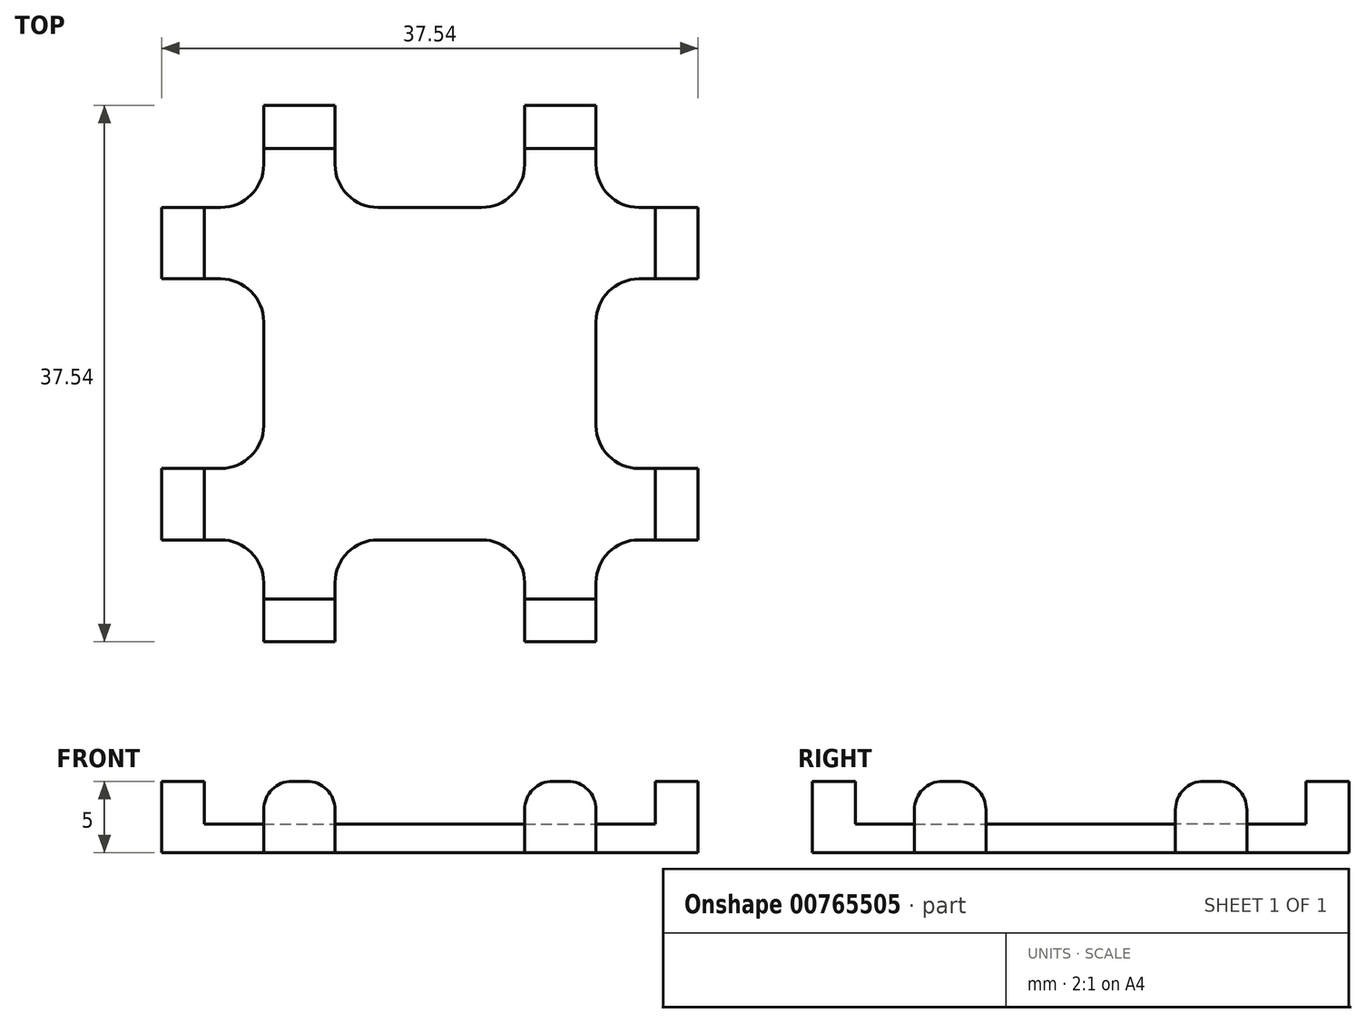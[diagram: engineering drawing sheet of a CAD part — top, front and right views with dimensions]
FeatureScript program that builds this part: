
annotation { "Feature Type Name" : "Feature", "Feature Type Description" : "" }
export const myFeature = defineFeature(function(context is Context, id is Id, definition is map)
    precondition{}
    {
        {
            var Q0;
            Q0=qCreatedBy(makeId("Top.planeOp"),FACE);
            var sketch = newSketch(context, id + "F0", { "sketchPlane" : qUnion([Q0])});
            skLineSegment(sketch, "E0", {"start": v(0, 0) * mm, "end": v(0, 13.26) * mm});
            skLineSegment(sketch, "E1", {"start": v(0, 13.26) * mm, "end": v(-7.14, 13.26) * mm});
            skLineSegment(sketch, "E2", {"start": v(-7.14, 13.26) * mm, "end": v(-7.14, 18.26) * mm});
            skLineSegment(sketch, "E3", {"start": v(-7.14, 18.26) * mm, "end": v(0, 18.26) * mm});
            skLineSegment(sketch, "E4", {"start": v(0, 18.26) * mm, "end": v(0, 25.4) * mm});
            skLineSegment(sketch, "E5", {"start": v(0, 25.4) * mm, "end": v(5, 25.4) * mm});
            skLineSegment(sketch, "E6", {"start": v(5, 25.4) * mm, "end": v(5, 18.26) * mm});
            skLineSegment(sketch, "E7", {"start": v(5, 18.26) * mm, "end": v(18.26, 18.26) * mm});
            skLineSegment(sketch, "E8", {"start": v(18.26, 18.26) * mm, "end": v(18.26, 25.4) * mm});
            skLineSegment(sketch, "E9", {"start": v(18.26, 25.4) * mm, "end": v(23.26, 25.4) * mm});
            skLineSegment(sketch, "E10", {"start": v(23.26, 25.4) * mm, "end": v(23.26, 18.26) * mm});
            skLineSegment(sketch, "E11", {"start": v(23.26, 18.26) * mm, "end": v(30.4, 18.26) * mm});
            skLineSegment(sketch, "E12", {"start": v(30.4, 18.26) * mm, "end": v(30.4, 13.26) * mm});
            skLineSegment(sketch, "E13", {"start": v(30.4, 13.26) * mm, "end": v(23.26, 13.26) * mm});
            skLineSegment(sketch, "E14", {"start": v(23.26, 13.26) * mm, "end": v(23.26, 0) * mm});
            skLineSegment(sketch, "E15", {"start": v(23.26, 0) * mm, "end": v(30.4, 0) * mm});
            skLineSegment(sketch, "E16", {"start": v(30.4, 0) * mm, "end": v(30.4, -5) * mm});
            skLineSegment(sketch, "E17", {"start": v(30.4, -5) * mm, "end": v(23.26, -5) * mm});
            skLineSegment(sketch, "E18", {"start": v(23.26, -5) * mm, "end": v(23.26, -12.14) * mm});
            skLineSegment(sketch, "E19", {"start": v(23.26, -12.14) * mm, "end": v(18.26, -12.14) * mm});
            skLineSegment(sketch, "E20", {"start": v(18.26, -12.14) * mm, "end": v(18.26, -5) * mm});
            skLineSegment(sketch, "E21", {"start": v(18.26, -5) * mm, "end": v(5, -5) * mm});
            skLineSegment(sketch, "E22", {"start": v(5, -5) * mm, "end": v(5, -12.14) * mm});
            skLineSegment(sketch, "E23", {"start": v(5, -12.14) * mm, "end": v(0, -12.14) * mm});
            skLineSegment(sketch, "E24", {"start": v(0, -5) * mm, "end": v(-7.14, -5) * mm});
            skLineSegment(sketch, "E25", {"start": v(-7.14, -5) * mm, "end": v(-7.14, 0) * mm});
            skLineSegment(sketch, "E26", {"start": v(-7.14, 0) * mm, "end": v(0, 0) * mm});
            skLineSegment(sketch, "E27", {"start": v(0, -5) * mm, "end": v(0, -12.14) * mm});
            skSolve(sketch);
        }
        {
            var Q0;
            Q0=makeQuery(id+"F0.imprint","IMPRINT",FACE,{"disambiguationData":[TD([[makeQuery(id+"F0.imprint","IMPRINT",EDGE,{"derivedFrom":sQuery(id+"F0.wireOp",EDGE,"E0")}),-1.0]])]});
            extrude(context, id + "F1", {"entities" : qUnion([Q0]), "depth" : 2 * mm, "offsetDistance" : 25 * mm});
        }
        {
            var Q0;
            Q0=makeQuery(id+"F1.opExtrude","CAP_FACE",FACE,{"disambiguationData":[OSD([sQuery(id+"F0.wireOp",EDGE,"E0"),sQuery(id+"F0.wireOp",EDGE,"E1"),sQuery(id+"F0.wireOp",EDGE,"E2"),sQuery(id+"F0.wireOp",EDGE,"E3"),sQuery(id+"F0.wireOp",EDGE,"E4"),sQuery(id+"F0.wireOp",EDGE,"E5"),sQuery(id+"F0.wireOp",EDGE,"E6"),sQuery(id+"F0.wireOp",EDGE,"E7"),sQuery(id+"F0.wireOp",EDGE,"E8"),sQuery(id+"F0.wireOp",EDGE,"E9"),sQuery(id+"F0.wireOp",EDGE,"E10"),sQuery(id+"F0.wireOp",EDGE,"E11"),sQuery(id+"F0.wireOp",EDGE,"E12"),sQuery(id+"F0.wireOp",EDGE,"E13"),sQuery(id+"F0.wireOp",EDGE,"E14"),sQuery(id+"F0.wireOp",EDGE,"E15"),sQuery(id+"F0.wireOp",EDGE,"E16"),sQuery(id+"F0.wireOp",EDGE,"E17"),sQuery(id+"F0.wireOp",EDGE,"E18"),sQuery(id+"F0.wireOp",EDGE,"E19"),sQuery(id+"F0.wireOp",EDGE,"E20"),sQuery(id+"F0.wireOp",EDGE,"E21"),sQuery(id+"F0.wireOp",EDGE,"E22"),sQuery(id+"F0.wireOp",EDGE,"E23"),sQuery(id+"F0.wireOp",EDGE,"E24"),sQuery(id+"F0.wireOp",EDGE,"E25"),sQuery(id+"F0.wireOp",EDGE,"E26"),sQuery(id+"F0.wireOp",EDGE,"E27")])],"isStart":false});
            var sketch = newSketch(context, id + "F2", { "sketchPlane" : qUnion([Q0])});
            skLineSegment(sketch, "E28.bottom", {"start": v(0, 25.4) * mm, "end": v(5, 25.4) * mm});
            skLineSegment(sketch, "E28.top", {"start": v(0, 22.4) * mm, "end": v(5, 22.4) * mm});
            skLineSegment(sketch, "E28.left", {"start": v(0, 25.4) * mm, "end": v(0, 22.4) * mm});
            skLineSegment(sketch, "E28.right", {"start": v(5, 25.4) * mm, "end": v(5, 22.4) * mm});
            skLineSegment(sketch, "E29.bottom", {"start": v(18.26, 25.4) * mm, "end": v(23.26, 25.4) * mm});
            skLineSegment(sketch, "E29.top", {"start": v(18.26, 22.4) * mm, "end": v(23.26, 22.4) * mm});
            skLineSegment(sketch, "E29.left", {"start": v(18.26, 25.4) * mm, "end": v(18.26, 22.4) * mm});
            skLineSegment(sketch, "E29.right", {"start": v(23.26, 25.4) * mm, "end": v(23.26, 22.4) * mm});
            skLineSegment(sketch, "E30.bottom", {"start": v(30.4, 18.26) * mm, "end": v(27.4, 18.26) * mm});
            skLineSegment(sketch, "E30.top", {"start": v(30.4, 13.26) * mm, "end": v(27.4, 13.26) * mm});
            skLineSegment(sketch, "E30.left", {"start": v(30.4, 18.26) * mm, "end": v(30.4, 13.26) * mm});
            skLineSegment(sketch, "E30.right", {"start": v(27.4, 18.26) * mm, "end": v(27.4, 13.26) * mm});
            skLineSegment(sketch, "E31.bottom", {"start": v(-7.14, 18.26) * mm, "end": v(-4.14, 18.26) * mm});
            skLineSegment(sketch, "E31.top", {"start": v(-7.14, 13.26) * mm, "end": v(-4.14, 13.26) * mm});
            skLineSegment(sketch, "E31.left", {"start": v(-7.14, 18.26) * mm, "end": v(-7.14, 13.26) * mm});
            skLineSegment(sketch, "E31.right", {"start": v(-4.14, 18.26) * mm, "end": v(-4.14, 13.26) * mm});
            skLineSegment(sketch, "E32.bottom", {"start": v(-7.14, 0) * mm, "end": v(-4.14, 0) * mm});
            skLineSegment(sketch, "E32.top", {"start": v(-7.14, -5) * mm, "end": v(-4.14, -5) * mm});
            skLineSegment(sketch, "E32.left", {"start": v(-7.14, 0) * mm, "end": v(-7.14, -5) * mm});
            skLineSegment(sketch, "E32.right", {"start": v(-4.14, 0) * mm, "end": v(-4.14, -5) * mm});
            skLineSegment(sketch, "E33.bottom", {"start": v(0, -12.14) * mm, "end": v(5, -12.14) * mm});
            skLineSegment(sketch, "E33.top", {"start": v(0, -9.14) * mm, "end": v(5, -9.14) * mm});
            skLineSegment(sketch, "E33.left", {"start": v(0, -12.14) * mm, "end": v(0, -9.14) * mm});
            skLineSegment(sketch, "E33.right", {"start": v(5, -12.14) * mm, "end": v(5, -9.14) * mm});
            skLineSegment(sketch, "E34.bottom", {"start": v(18.26, -12.14) * mm, "end": v(23.26, -12.14) * mm});
            skLineSegment(sketch, "E34.top", {"start": v(18.26, -9.14) * mm, "end": v(23.26, -9.14) * mm});
            skLineSegment(sketch, "E34.left", {"start": v(18.26, -12.14) * mm, "end": v(18.26, -9.14) * mm});
            skLineSegment(sketch, "E34.right", {"start": v(23.26, -12.14) * mm, "end": v(23.26, -9.14) * mm});
            skLineSegment(sketch, "E35.bottom", {"start": v(30.4, -5) * mm, "end": v(27.4, -5) * mm});
            skLineSegment(sketch, "E35.top", {"start": v(30.4, 0) * mm, "end": v(27.4, 0) * mm});
            skLineSegment(sketch, "E35.left", {"start": v(30.4, -5) * mm, "end": v(30.4, 0) * mm});
            skLineSegment(sketch, "E35.right", {"start": v(27.4, -5) * mm, "end": v(27.4, 0) * mm});
            skSolve(sketch);
        }
        {
            var Q0;
            Q0=makeQuery(id+"F2.imprint","IMPRINT",FACE,{"disambiguationData":[TD([[makeQuery(id+"F2.imprint","IMPRINT",EDGE,{"derivedFrom":sQuery(id+"F2.wireOp",EDGE,"E28.bottom")}),-1.0]])]});
            var Q1;
            Q1=makeQuery(id+"F2.imprint","IMPRINT",FACE,{"disambiguationData":[TD([[makeQuery(id+"F2.imprint","IMPRINT",EDGE,{"derivedFrom":sQuery(id+"F2.wireOp",EDGE,"E29.bottom")}),-1.0]])]});
            var Q2;
            Q2=makeQuery(id+"F2.imprint","IMPRINT",FACE,{"disambiguationData":[TD([[makeQuery(id+"F2.imprint","IMPRINT",EDGE,{"derivedFrom":sQuery(id+"F2.wireOp",EDGE,"E31.bottom")}),-1.0]])]});
            var Q3;
            Q3=makeQuery(id+"F2.imprint","IMPRINT",FACE,{"disambiguationData":[TD([[makeQuery(id+"F2.imprint","IMPRINT",EDGE,{"derivedFrom":sQuery(id+"F2.wireOp",EDGE,"E30.bottom")}),-1.0]])]});
            var Q4;
            Q4=makeQuery(id+"F2.imprint","IMPRINT",FACE,{"disambiguationData":[TD([[makeQuery(id+"F2.imprint","IMPRINT",EDGE,{"derivedFrom":sQuery(id+"F2.wireOp",EDGE,"E35.bottom")}),-1.0]])]});
            var Q5;
            Q5=makeQuery(id+"F2.imprint","IMPRINT",FACE,{"disambiguationData":[TD([[makeQuery(id+"F2.imprint","IMPRINT",EDGE,{"derivedFrom":sQuery(id+"F2.wireOp",EDGE,"E34.bottom")}),-1.0]])]});
            var Q6;
            Q6=makeQuery(id+"F2.imprint","IMPRINT",FACE,{"disambiguationData":[TD([[makeQuery(id+"F2.imprint","IMPRINT",EDGE,{"derivedFrom":sQuery(id+"F2.wireOp",EDGE,"E33.bottom")}),-1.0]])]});
            var Q7;
            Q7=makeQuery(id+"F2.imprint","IMPRINT",FACE,{"disambiguationData":[TD([[makeQuery(id+"F2.imprint","IMPRINT",EDGE,{"derivedFrom":sQuery(id+"F2.wireOp",EDGE,"E32.bottom")}),-1.0]])]});
            extrude(context, id + "F3", {"entities" : qUnion([Q0, Q1, Q2, Q3, Q4, Q5, Q6, Q7]), "operationType" : NewBodyOperationType.ADD, "depth" : 3 * mm, "offsetDistance" : 25 * mm});
        }
        {
            var Q0;
            Q0=makeQuery(id+"F1.opExtrude","SWEPT_EDGE",EDGE,{"disambiguationData":[OSD([sQuery(id+"F0.wireOp",EDGE,"E7"),sQuery(id+"F0.wireOp",EDGE,"E8")])]});
            var Q1;
            Q1=makeQuery(id+"F1.opExtrude","SWEPT_EDGE",EDGE,{"disambiguationData":[OSD([sQuery(id+"F0.wireOp",EDGE,"E6"),sQuery(id+"F0.wireOp",EDGE,"E7")])]});
            var Q2;
            Q2=makeQuery(id+"F1.opExtrude","SWEPT_EDGE",EDGE,{"disambiguationData":[OSD([sQuery(id+"F0.wireOp",EDGE,"E3"),sQuery(id+"F0.wireOp",EDGE,"E4")])]});
            var Q3;
            Q3=makeQuery(id+"F1.opExtrude","SWEPT_EDGE",EDGE,{"disambiguationData":[OSD([sQuery(id+"F0.wireOp",EDGE,"E0"),sQuery(id+"F0.wireOp",EDGE,"E1")])]});
            var Q4;
            Q4=makeQuery(id+"F1.opExtrude","SWEPT_EDGE",EDGE,{"disambiguationData":[OSD([sQuery(id+"F0.wireOp",EDGE,"E0"),sQuery(id+"F0.wireOp",EDGE,"E26")])]});
            var Q5;
            Q5=makeQuery(id+"F1.opExtrude","SWEPT_EDGE",EDGE,{"disambiguationData":[OSD([sQuery(id+"F0.wireOp",EDGE,"E24"),sQuery(id+"F0.wireOp",EDGE,"E27")])]});
            var Q6;
            Q6=makeQuery(id+"F1.opExtrude","SWEPT_EDGE",EDGE,{"disambiguationData":[OSD([sQuery(id+"F0.wireOp",EDGE,"E21"),sQuery(id+"F0.wireOp",EDGE,"E22")])]});
            var Q7;
            Q7=makeQuery(id+"F1.opExtrude","SWEPT_EDGE",EDGE,{"disambiguationData":[OSD([sQuery(id+"F0.wireOp",EDGE,"E20"),sQuery(id+"F0.wireOp",EDGE,"E21")])]});
            var Q8;
            Q8=makeQuery(id+"F1.opExtrude","SWEPT_EDGE",EDGE,{"disambiguationData":[OSD([sQuery(id+"F0.wireOp",EDGE,"E17"),sQuery(id+"F0.wireOp",EDGE,"E18")])]});
            var Q9;
            Q9=makeQuery(id+"F1.opExtrude","SWEPT_EDGE",EDGE,{"disambiguationData":[OSD([sQuery(id+"F0.wireOp",EDGE,"E13"),sQuery(id+"F0.wireOp",EDGE,"E14")])]});
            var Q10;
            Q10=makeQuery(id+"F1.opExtrude","SWEPT_EDGE",EDGE,{"disambiguationData":[OSD([sQuery(id+"F0.wireOp",EDGE,"E14"),sQuery(id+"F0.wireOp",EDGE,"E15")])]});
            var Q11;
            Q11=makeQuery(id+"F1.opExtrude","SWEPT_EDGE",EDGE,{"disambiguationData":[OSD([sQuery(id+"F0.wireOp",EDGE,"E10"),sQuery(id+"F0.wireOp",EDGE,"E11")])]});
            fillet(context, id + "F4", {"entities" : qUnion([Q0, Q1, Q2, Q3, Q4, Q5, Q6, Q7, Q8, Q9, Q10, Q11]), "radius" : 3 * mm, "tangentPropagation" : true, "allowEdgeOverflow" : false});
        }
        {
            var Q0;
            Q0=makeQuery(id+"F3.opExtrude","CAP_EDGE",EDGE,{"disambiguationData":[OSD([sQuery(id+"F2.wireOp",EDGE,"E32.top")])],"isStart":false});
            var Q1;
            Q1=makeQuery(id+"F3.opExtrude","CAP_EDGE",EDGE,{"disambiguationData":[OSD([sQuery(id+"F2.wireOp",EDGE,"E32.bottom")])],"isStart":false});
            var Q2;
            Q2=makeQuery(id+"F3.opExtrude","CAP_EDGE",EDGE,{"disambiguationData":[OSD([sQuery(id+"F2.wireOp",EDGE,"E31.top")])],"isStart":false});
            var Q3;
            Q3=makeQuery(id+"F3.opExtrude","CAP_EDGE",EDGE,{"disambiguationData":[OSD([sQuery(id+"F2.wireOp",EDGE,"E31.bottom")])],"isStart":false});
            var Q4;
            Q4=makeQuery(id+"F3.opExtrude","CAP_EDGE",EDGE,{"disambiguationData":[OSD([sQuery(id+"F2.wireOp",EDGE,"E28.left")])],"isStart":false});
            var Q5;
            Q5=makeQuery(id+"F3.opExtrude","CAP_EDGE",EDGE,{"disambiguationData":[OSD([sQuery(id+"F2.wireOp",EDGE,"E28.right")])],"isStart":false});
            var Q6;
            Q6=makeQuery(id+"F3.opExtrude","CAP_EDGE",EDGE,{"disambiguationData":[OSD([sQuery(id+"F2.wireOp",EDGE,"E29.left")])],"isStart":false});
            var Q7;
            Q7=makeQuery(id+"F3.opExtrude","CAP_EDGE",EDGE,{"disambiguationData":[OSD([sQuery(id+"F2.wireOp",EDGE,"E29.right")])],"isStart":false});
            var Q8;
            Q8=makeQuery(id+"F3.opExtrude","CAP_EDGE",EDGE,{"disambiguationData":[OSD([sQuery(id+"F2.wireOp",EDGE,"E30.top")])],"isStart":false});
            var Q9;
            Q9=makeQuery(id+"F3.opExtrude","CAP_EDGE",EDGE,{"disambiguationData":[OSD([sQuery(id+"F2.wireOp",EDGE,"E30.bottom")])],"isStart":false});
            var Q10;
            Q10=makeQuery(id+"F3.opExtrude","CAP_EDGE",EDGE,{"disambiguationData":[OSD([sQuery(id+"F2.wireOp",EDGE,"E35.bottom")])],"isStart":false});
            var Q11;
            Q11=makeQuery(id+"F3.opExtrude","CAP_EDGE",EDGE,{"disambiguationData":[OSD([sQuery(id+"F2.wireOp",EDGE,"E35.top")])],"isStart":false});
            var Q12;
            Q12=makeQuery(id+"F3.opExtrude","CAP_EDGE",EDGE,{"disambiguationData":[OSD([sQuery(id+"F2.wireOp",EDGE,"E34.right")])],"isStart":false});
            var Q13;
            Q13=makeQuery(id+"F3.opExtrude","CAP_EDGE",EDGE,{"disambiguationData":[OSD([sQuery(id+"F2.wireOp",EDGE,"E34.left")])],"isStart":false});
            var Q14;
            Q14=makeQuery(id+"F3.opExtrude","CAP_EDGE",EDGE,{"disambiguationData":[OSD([sQuery(id+"F2.wireOp",EDGE,"E33.right")])],"isStart":false});
            var Q15;
            Q15=makeQuery(id+"F3.opExtrude","CAP_EDGE",EDGE,{"disambiguationData":[OSD([sQuery(id+"F2.wireOp",EDGE,"E33.left")])],"isStart":false});
            fillet(context, id + "F5", {"entities" : qUnion([Q0, Q1, Q2, Q3, Q4, Q5, Q6, Q7, Q8, Q9, Q10, Q11, Q12, Q13, Q14, Q15]), "radius" : 2 * mm, "tangentPropagation" : true, "allowEdgeOverflow" : false});
        }
    });
